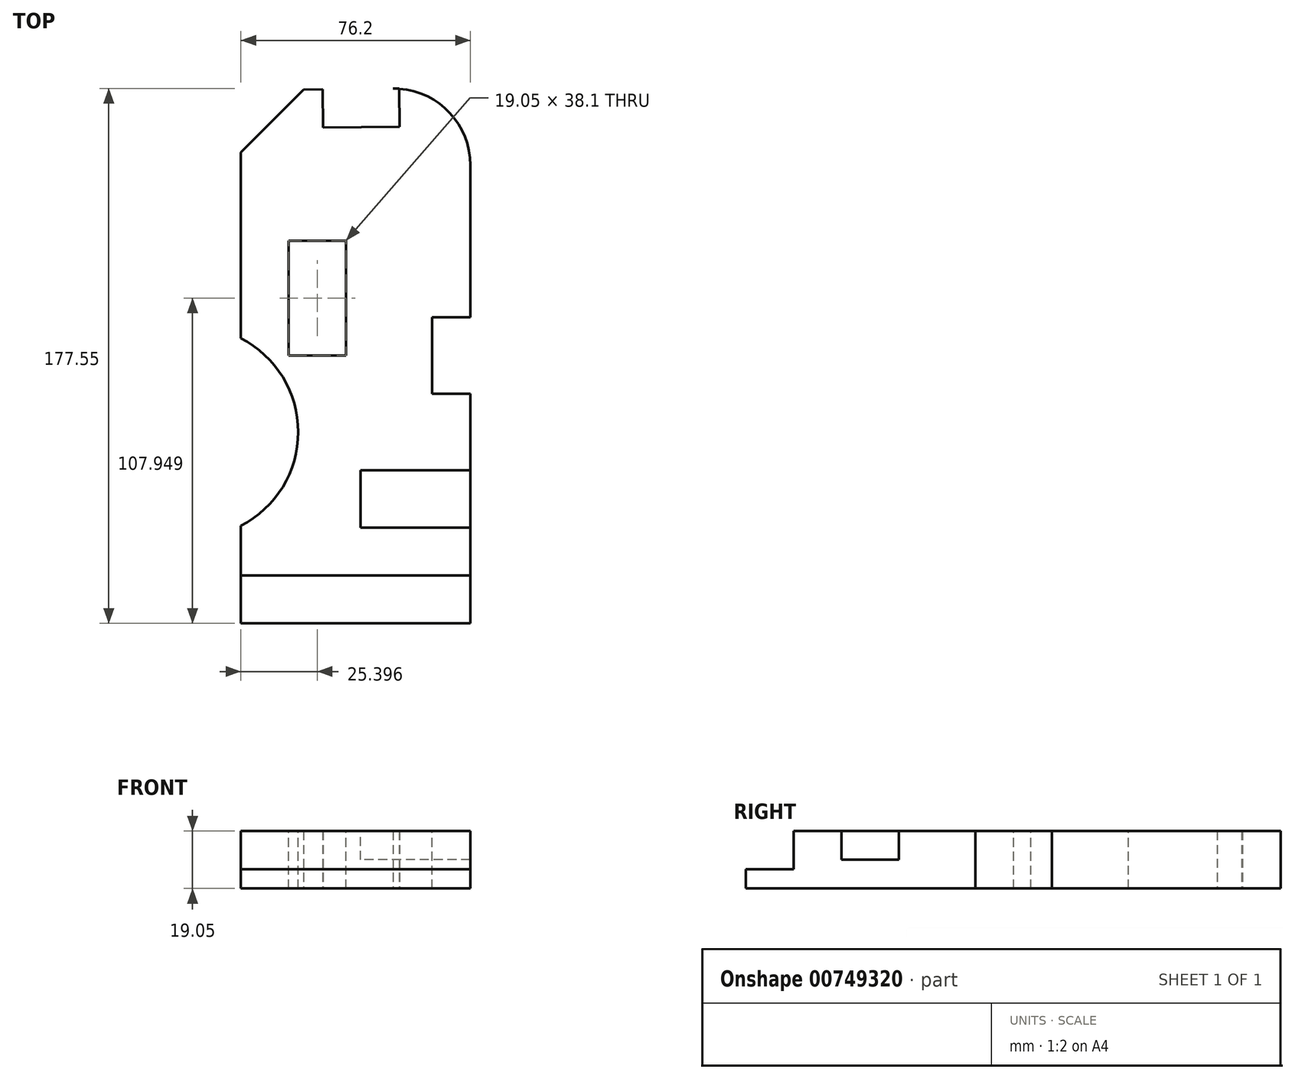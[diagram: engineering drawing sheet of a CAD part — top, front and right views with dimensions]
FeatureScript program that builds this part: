
annotation { "Feature Type Name" : "Feature", "Feature Type Description" : "" }
export const myFeature = defineFeature(function(context is Context, id is Id, definition is map)
    precondition{}
    {
        {
            var Q0;
            Q0=qCreatedBy(makeId("Top.planeOp"),FACE);
            var sketch = newSketch(context, id + "F0", { "sketchPlane" : qUnion([Q0])});
            skLineSegment(sketch, "E0", {"start": v(-42.47, 109.73) * mm, "end": v(-42.47, -46.63) * mm});
            skLineSegment(sketch, "E1", {"start": v(-42.47, -46.63) * mm, "end": v(33.73, -46.63) * mm});
            skLineSegment(sketch, "E2", {"start": v(33.73, -46.63) * mm, "end": v(33.73, 105.5) * mm});
            skLineSegment(sketch, "E3", {"start": v(-21.62, 130.59) * mm, "end": v(-15.27, 130.65) * mm});
            skLineSegment(sketch, "E4", {"start": v(-42.47, 109.73) * mm, "end": v(-21.62, 130.59) * mm});
            skLineSegment(sketch, "E5", {"start": v(-15.27, 130.65) * mm, "end": v(-15.13, 117.95) * mm});
            skLineSegment(sketch, "E6", {"start": v(-15.13, 117.95) * mm, "end": v(10.26, 118.22) * mm});
            skLineSegment(sketch, "E7", {"start": v(10.26, 118.22) * mm, "end": v(10.13, 130.92) * mm});
            skLineSegment(sketch, "E8.trimOffspring", {"start": v(8.06, 130.9) * mm, "end": v(10.13, 130.92) * mm});
            skPoint(sketch, "E9.visualSharp", {"position": v(33.73, 131.17) * mm});
            skArc(sketch, "E9.filletArc", {"start": v(33.73, 105.5) * mm, "mid": v(26.2, 123.56) * mm, "end": v(8.06, 130.9) * mm});
            skSolve(sketch);
        }
        {
            var Q0;
            Q0 = qSketchRegion(id + "F0", true);
            extrude(context, id + "F1", {"entities" : qUnion([Q0]), "depth" : 19.05 * mm, "offsetDistance" : 25.4 * mm});
        }
        {
            var Q0;
            Q0=makeQuery(id+"F1.opExtrude","SWEPT_FACE",FACE,{"disambiguationData":[OSD([sQuery(id+"F0.wireOp",EDGE,"E1")])]});
            var sketch = newSketch(context, id + "F2", { "sketchPlane" : qUnion([Q0])});
            skLineSegment(sketch, "E10", {"start": v(-42.47, 0) * mm, "end": v(-42.47, 6.35) * mm});
            skLineSegment(sketch, "E11", {"start": v(-42.47, 6.35) * mm, "end": v(33.73, 6.35) * mm});
            skSolve(sketch);
        }
        {
            var Q0;
            Q0 = qSketchRegion(id + "F2", true);
            var Q1;
            {var subQ0=sQuery(id+"F2.wireOp",EDGE,"E11");Q1=makeQuery(id+"F2.imprint","IMPRINT",FACE,{"disambiguationData":[TD([[makeQuery(id+"F2.imprint","IMPRINT",EDGE,{"derivedFrom":subQ0}),1.0]])]});}
            extrude(context, id + "F3", {"entities" : qUnion([Q0, Q1]), "operationType" : NewBodyOperationType.REMOVE, "oppositeDirection" : true, "depth" : 15.88 * mm, "offsetDistance" : 25.4 * mm});
        }
        {
            var Q0;
            Q0=makeQuery(id+"F1.opExtrude","CAP_FACE",FACE,{"disambiguationData":[OSD([sQuery(id+"F0.wireOp",EDGE,"E0"),sQuery(id+"F0.wireOp",EDGE,"E1"),sQuery(id+"F0.wireOp",EDGE,"E2"),sQuery(id+"F0.wireOp",EDGE,"E4"),sQuery(id+"F0.wireOp",EDGE,"E3"),sQuery(id+"F0.wireOp",EDGE,"E5"),sQuery(id+"F0.wireOp",EDGE,"E6"),sQuery(id+"F0.wireOp",EDGE,"E7"),sQuery(id+"F0.wireOp",EDGE,"E9.filletArc")])],"isStart":false});
            var sketch = newSketch(context, id + "F4", { "sketchPlane" : qUnion([Q0])});
            skLineSegment(sketch, "E12", {"start": v(-42.47, -30.76) * mm, "end": v(-42.47, -14.88) * mm});
            skLineSegment(sketch, "E13", {"start": v(-42.47, -14.88) * mm, "end": v(-42.47, 16.87) * mm});
            skLineSegment(sketch, "E14", {"start": v(-42.47, 16.87) * mm, "end": v(-23.42, 16.87) * mm});
            skArc(sketch, "E15", {"start": v(-42.47, -14.24) * mm, "mid": v(-23.42, 16.87) * mm, "end": v(-42.47, 47.98) * mm});
            skLineSegment(sketch, "E16", {"start": v(-42.47, 16.87) * mm, "end": v(-42.47, 47.98) * mm});
            skSolve(sketch);
        }
        {
            var Q0;
            Q0 = qSketchRegion(id + "F4", true);
            extrude(context, id + "F5", {"entities" : qUnion([Q0]), "operationType" : NewBodyOperationType.REMOVE, "oppositeDirection" : true, "depth" : 25.4 * mm, "offsetDistance" : 25.4 * mm});
        }
        {
            var Q0;
            Q0=makeQuery(id+"F1.opExtrude","CAP_FACE",FACE,{"disambiguationData":[OSD([sQuery(id+"F0.wireOp",EDGE,"E0"),sQuery(id+"F0.wireOp",EDGE,"E1"),sQuery(id+"F0.wireOp",EDGE,"E2"),sQuery(id+"F0.wireOp",EDGE,"E4"),sQuery(id+"F0.wireOp",EDGE,"E3"),sQuery(id+"F0.wireOp",EDGE,"E5"),sQuery(id+"F0.wireOp",EDGE,"E6"),sQuery(id+"F0.wireOp",EDGE,"E7"),sQuery(id+"F0.wireOp",EDGE,"E9.filletArc")])],"isStart":false});
            var sketch = newSketch(context, id + "F6", { "sketchPlane" : qUnion([Q0])});
            skLineSegment(sketch, "E17", {"start": v(33.73, -30.76) * mm, "end": v(33.73, -14.88) * mm});
            skLineSegment(sketch, "E18", {"start": v(33.73, -14.88) * mm, "end": v(-2.79, -14.88) * mm});
            skLineSegment(sketch, "E19", {"start": v(-2.79, -14.88) * mm, "end": v(-2.79, 4.17) * mm});
            skLineSegment(sketch, "E20", {"start": v(-2.79, 4.17) * mm, "end": v(33.73, 4.17) * mm});
            skSolve(sketch);
        }
        {
            var Q0;
            Q0 = qSketchRegion(id + "F6", true);
            var Q1;
            {var subQ0=sQuery(id+"F6.wireOp",EDGE,"E18");Q1=makeQuery(id+"F6.imprint","IMPRINT",FACE,{"disambiguationData":[TD([[makeQuery(id+"F6.imprint","IMPRINT",EDGE,{"derivedFrom":subQ0}),-1.0]])]});}
            extrude(context, id + "F7", {"entities" : qUnion([Q0, Q1]), "operationType" : NewBodyOperationType.REMOVE, "oppositeDirection" : true, "depth" : 9.52 * mm, "offsetDistance" : 25.4 * mm});
        }
        {
            var Q0;
            Q0=makeQuery(id+"F1.opExtrude","CAP_FACE",FACE,{"disambiguationData":[OSD([sQuery(id+"F0.wireOp",EDGE,"E0"),sQuery(id+"F0.wireOp",EDGE,"E1"),sQuery(id+"F0.wireOp",EDGE,"E2"),sQuery(id+"F0.wireOp",EDGE,"E4"),sQuery(id+"F0.wireOp",EDGE,"E3"),sQuery(id+"F0.wireOp",EDGE,"E5"),sQuery(id+"F0.wireOp",EDGE,"E6"),sQuery(id+"F0.wireOp",EDGE,"E7"),sQuery(id+"F0.wireOp",EDGE,"E9.filletArc")])],"isStart":false});
            var sketch = newSketch(context, id + "F8", { "sketchPlane" : qUnion([Q0])});
            skLineSegment(sketch, "E21", {"start": v(33.73, 4.17) * mm, "end": v(33.73, 29.57) * mm});
            skLineSegment(sketch, "E22", {"start": v(33.73, 29.57) * mm, "end": v(21.03, 29.57) * mm});
            skLineSegment(sketch, "E23", {"start": v(21.03, 29.57) * mm, "end": v(21.03, 54.97) * mm});
            skLineSegment(sketch, "E24", {"start": v(21.03, 54.97) * mm, "end": v(33.73, 54.97) * mm});
            skLineSegment(sketch, "E25", {"start": v(2.56, 4.17) * mm, "end": v(2.56, 42.27) * mm});
            skLineSegment(sketch, "E26", {"start": v(-42.47, 50.91) * mm, "end": v(-26.6, 50.91) * mm});
            skLineSegment(sketch, "E27", {"start": v(-26.6, 42.27) * mm, "end": v(-26.6, 80.37) * mm});
            skLineSegment(sketch, "E28", {"start": v(-26.6, 80.37) * mm, "end": v(-7.55, 80.37) * mm});
            skLineSegment(sketch, "E29", {"start": v(-7.55, 80.37) * mm, "end": v(-7.55, 42.27) * mm});
            skLineSegment(sketch, "E30", {"start": v(-7.55, 42.27) * mm, "end": v(-26.6, 42.27) * mm});
            skSolve(sketch);
        }
        {
            var Q0;
            Q0 = qSketchRegion(id + "F8", true);
            var Q1;
            {var subQ0=sQuery(id+"F8.wireOp",EDGE,"E22");Q1=makeQuery(id+"F8.imprint","IMPRINT",FACE,{"disambiguationData":[TD([[makeQuery(id+"F8.imprint","IMPRINT",EDGE,{"derivedFrom":subQ0}),-1.0]])]});}
            extrude(context, id + "F9", {"entities" : qUnion([Q0, Q1]), "operationType" : NewBodyOperationType.REMOVE, "oppositeDirection" : true, "depth" : 25.4 * mm, "offsetDistance" : 25.4 * mm});
        }
    });
